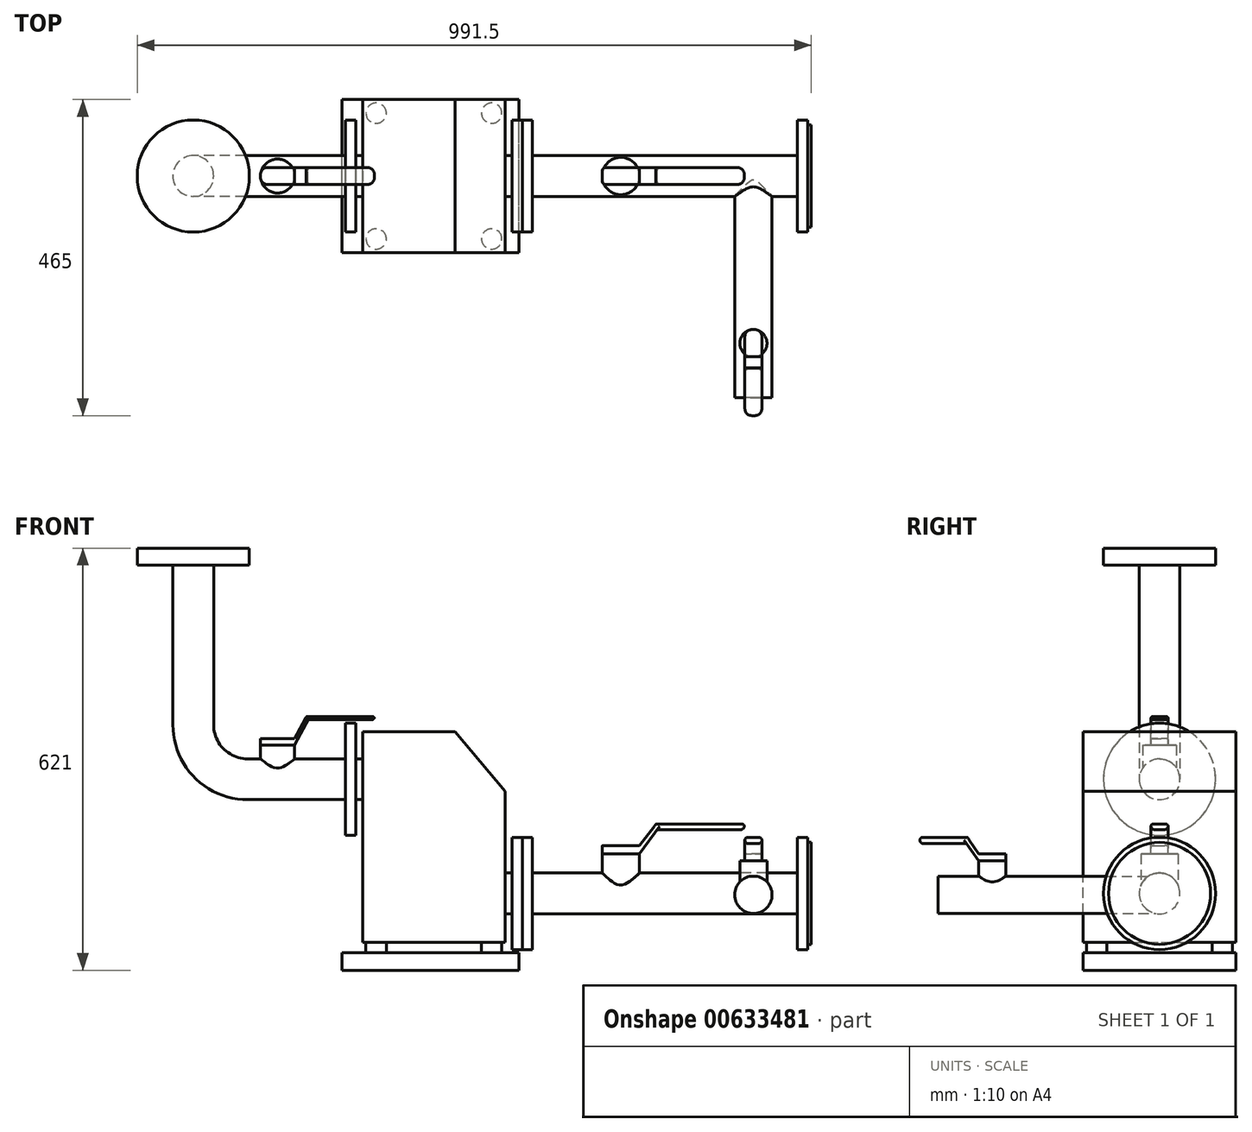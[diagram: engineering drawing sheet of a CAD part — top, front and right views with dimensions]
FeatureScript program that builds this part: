
annotation { "Feature Type Name" : "Feature", "Feature Type Description" : "" }
export const myFeature = defineFeature(function(context is Context, id is Id, definition is map)
    precondition{}
    {
        {
            var Q0;
            Q0=qCreatedBy(makeId("Front.planeOp"),FACE);
            var sketch = newSketch(context, id + "F0", { "sketchPlane" : qUnion([Q0])});
            skLineSegment(sketch, "E0.bottom", {"start": v(0, 0) * mm, "end": v(210, 0) * mm});
            skLineSegment(sketch, "E0.top", {"start": v(0, 310) * mm, "end": v(136.03, 310) * mm});
            skLineSegment(sketch, "E0.left", {"start": v(0, 0) * mm, "end": v(0, 310) * mm});
            skLineSegment(sketch, "E0.right", {"start": v(210, 0) * mm, "end": v(210, 222.5) * mm});
            skLineSegment(sketch, "E1", {"start": v(136.03, 310) * mm, "end": v(210, 222.5) * mm});
            skSolve(sketch);
        }
        {
            var Q0;
            Q0=makeQuery(id+"F0.imprint","IMPRINT",FACE,{"disambiguationData":[TD([[makeQuery(id+"F0.imprint","IMPRINT",EDGE,{"derivedFrom":sQuery(id+"F0.wireOp",EDGE,"E0.bottom")}),1.0]])]});
            extrude(context, id + "F1", {"entities" : qUnion([Q0]), "depth" : 225 * mm, "offsetDistance" : 25 * mm});
        }
        {
            var Q0;
            Q0=makeQuery(id+"F1.opExtrude","SWEPT_FACE",FACE,{"disambiguationData":[OSD([sQuery(id+"F0.wireOp",EDGE,"E0.right")])]});
            var sketch = newSketch(context, id + "F2", { "sketchPlane" : qUnion([Q0])});
            skCircle(sketch, "E2", {"center": v(-112.5, 72.05) * mm, "radius": 30 * mm});
            skPoint(sketch, "E2.centerSnap0", {"position": v(-112.5, 0) * mm});
            skCircle(sketch, "E3", {"center": v(-112.5, 72.05) * mm, "radius": 82.5 * mm});
            skSolve(sketch);
        }
        {
            var Q0;
            Q0=makeQuery(id+"F2.imprint","IMPRINT",FACE,{"disambiguationData":[TD([[makeQuery(id+"F2.imprint","IMPRINT",EDGE,{"derivedFrom":sQuery(id+"F2.wireOp",EDGE,"E2")}),1.0]])]});
            extrude(context, id + "F3", {"entities" : qUnion([Q0]), "operationType" : NewBodyOperationType.ADD, "depth" : 10 * mm, "offsetDistance" : 25 * mm});
        }
        {
            var Q0;
            Q0=makeQuery(id+"F3.opExtrude","CAP_FACE",FACE,{"disambiguationData":[OSD([sQuery(id+"F2.wireOp",EDGE,"E2")])],"isStart":false});
            var sketch = newSketch(context, id + "F4", { "sketchPlane" : qUnion([Q0])});
            skCircle(sketch, "E4", {"center": v(-112.5, 72.05) * mm, "radius": 82.5 * mm});
            skSolve(sketch);
        }
        {
            var Q0;
            Q0=makeQuery(id+"F4.imprint","IMPRINT",FACE,{"disambiguationData":[TD([[makeQuery(id+"F4.imprint","IMPRINT",EDGE,{"derivedFrom":sQuery(id+"F4.wireOp",EDGE,"E4")}),1.0]])]});
            var Q1;
            Q1=makeQuery(id+"F4.imprint","IMPRINT",FACE,{"disambiguationData":[TD([[makeQuery(id+"F4.imprint","IMPRINT",EDGE,{"derivedFrom":makeQuery(id+"F3.opExtrude","CAP_EDGE",EDGE,{"disambiguationData":[OSD([sQuery(id+"F2.wireOp",EDGE,"E2")])],"isStart":false})}),1.0]])]});
            extrude(context, id + "F5", {"entities" : qUnion([Q0, Q1]), "operationType" : NewBodyOperationType.ADD, "depth" : 15 * mm, "offsetDistance" : 25 * mm});
        }
        {
            var Q0;
            Q0=makeQuery(id+"F1.opExtrude","SWEPT_FACE",FACE,{"disambiguationData":[OSD([sQuery(id+"F0.wireOp",EDGE,"E0.left")])]});
            var sketch = newSketch(context, id + "F6", { "sketchPlane" : qUnion([Q0])});
            skCircle(sketch, "E5", {"center": v(112.5, 240) * mm, "radius": 30 * mm});
            skPoint(sketch, "E5.centerSnap0", {"position": v(112.5, 0) * mm});
            skSolve(sketch);
        }
        {
            var Q0;
            Q0=makeQuery(id+"F6.imprint","IMPRINT",FACE,{"disambiguationData":[TD([[makeQuery(id+"F6.imprint","IMPRINT",EDGE,{"derivedFrom":sQuery(id+"F6.wireOp",EDGE,"E5")}),1.0]])]});
            extrude(context, id + "F7", {"entities" : qUnion([Q0]), "operationType" : NewBodyOperationType.ADD, "depth" : 10 * mm, "offsetDistance" : 25 * mm});
        }
        {
            var Q0;
            Q0=makeQuery(id+"F7.opExtrude","CAP_FACE",FACE,{"disambiguationData":[OSD([sQuery(id+"F6.wireOp",EDGE,"E5")])],"isStart":false});
            var sketch = newSketch(context, id + "F8", { "sketchPlane" : qUnion([Q0])});
            skCircle(sketch, "E6", {"center": v(112.5, 240) * mm, "radius": 82.5 * mm});
            skSolve(sketch);
        }
        {
            var Q0;
            Q0 = qSketchRegion(id + "F8", true);
            extrude(context, id + "F9", {"entities" : qUnion([Q0]), "operationType" : NewBodyOperationType.ADD, "depth" : 15 * mm, "offsetDistance" : 25 * mm});
        }
        {
            var Q0;
            Q0=makeQuery(id+"F1.opExtrude","SWEPT_FACE",FACE,{"disambiguationData":[OSD([sQuery(id+"F0.wireOp",EDGE,"E0.bottom")])]});
            var sketch = newSketch(context, id + "F10", { "sketchPlane" : qUnion([Q0])});
            skCircle(sketch, "E7", {"center": v(20, 205) * mm, "radius": 15 * mm});
            skCircle(sketch, "E8.0.1.0", {"center": v(20, 20) * mm, "radius": 15 * mm});
            skCircle(sketch, "E8.1.0.0", {"center": v(190, 205) * mm, "radius": 15 * mm});
            skCircle(sketch, "E8.1.1.0", {"center": v(190, 20) * mm, "radius": 15 * mm});
            skLineSegment(sketch, "E8.direction1", {"start": v(20, 205) * mm, "end": v(190, 205) * mm, "construction": true});
            skLineSegment(sketch, "E8.direction2", {"start": v(20, 205) * mm, "end": v(20, 20) * mm, "construction": true});
            skSolve(sketch);
        }
        {
            var Q0;
            Q0 = qSketchRegion(id + "F10", true);
            extrude(context, id + "F11", {"entities" : qUnion([Q0]), "operationType" : NewBodyOperationType.ADD, "depth" : 15 * mm, "offsetDistance" : 25 * mm});
        }
        {
            var Q0;
            Q0=makeQuery(id+"F11.opExtrude","CAP_FACE",FACE,{"disambiguationData":[OSD([sQuery(id+"F10.wireOp",EDGE,"E7")])],"isStart":false});
            var sketch = newSketch(context, id + "F12", { "sketchPlane" : qUnion([Q0])});
            skPoint(sketch, "E9.bottom.start.orphan", {"position": v(0, 70.5) * mm});
            skLineSegment(sketch, "E10.bottom", {"start": v(-30, 225) * mm, "end": v(230, 225) * mm});
            skLineSegment(sketch, "E10.top", {"start": v(-30, 0) * mm, "end": v(230, 0) * mm});
            skLineSegment(sketch, "E10.left", {"start": v(-30, 225) * mm, "end": v(-30, 0) * mm});
            skLineSegment(sketch, "E10.right", {"start": v(230, 225) * mm, "end": v(230, 0) * mm});
            skSolve(sketch);
        }
        {
            var Q0;
            Q0 = qSketchRegion(id + "F12", true);
            extrude(context, id + "F13", {"entities" : qUnion([Q0]), "operationType" : NewBodyOperationType.ADD, "depth" : 26 * mm, "offsetDistance" : 25 * mm});
        }
        {
            var Q0;
            Q0=makeQuery(id+"F5.opExtrude","CAP_FACE",FACE,{"disambiguationData":[OSD([sQuery(id+"F4.wireOp",EDGE,"E4")])],"isStart":false});
            var sketch = newSketch(context, id + "F14", { "sketchPlane" : qUnion([Q0])});
            skCircle(sketch, "E11", {"center": v(-112.5, 72.05) * mm, "radius": 82.5 * mm});
            skSolve(sketch);
        }
        {
            var Q0;
            Q0=makeQuery(id+"F14.imprint","IMPRINT",FACE,{"disambiguationData":[TD([[makeQuery(id+"F14.imprint","IMPRINT",EDGE,{"derivedFrom":sQuery(id+"F14.wireOp",EDGE,"E11")}),1.0]])]});
            extrude(context, id + "F15", {"entities" : qUnion([Q0]), "depth" : 15 * mm, "offsetDistance" : 25 * mm});
        }
        {
            var Q0;
            Q0=makeQuery(id+"F15.opExtrude","CAP_FACE",FACE,{"disambiguationData":[OSD([sQuery(id+"F14.wireOp",EDGE,"E11")])],"isStart":false});
            var sketch = newSketch(context, id + "F16", { "sketchPlane" : qUnion([Q0])});
            skCircle(sketch, "E12", {"center": v(-112.5, 72.05) * mm, "radius": 30 * mm});
            skSolve(sketch);
        }
        {
            var Q0;
            Q0=makeQuery(id+"F16.imprint","IMPRINT",FACE,{"disambiguationData":[TD([[makeQuery(id+"F16.imprint","IMPRINT",EDGE,{"derivedFrom":sQuery(id+"F16.wireOp",EDGE,"E12")}),1.0]])]});
            extrude(context, id + "F17", {"entities" : qUnion([Q0]), "operationType" : NewBodyOperationType.ADD, "depth" : 390 * mm, "offsetDistance" : 25 * mm});
        }
        {
            var Q0;
            Q0=makeQuery(id+"F17.opExtrude","CAP_FACE",FACE,{"disambiguationData":[OSD([sQuery(id+"F16.wireOp",EDGE,"E12")])],"isStart":false});
            var sketch = newSketch(context, id + "F18", { "sketchPlane" : qUnion([Q0])});
            skCircle(sketch, "E13", {"center": v(-112.5, 72.05) * mm, "radius": 82.5 * mm});
            skSolve(sketch);
        }
        {
            var Q0;
            Q0=makeQuery(id+"F18.imprint","IMPRINT",FACE,{"disambiguationData":[TD([[makeQuery(id+"F18.imprint","IMPRINT",EDGE,{"derivedFrom":sQuery(id+"F18.wireOp",EDGE,"E13")}),1.0]])]});
            var Q1;
            Q1=makeQuery(id+"F18.imprint","IMPRINT",FACE,{"disambiguationData":[TD([[makeQuery(id+"F18.imprint","IMPRINT",EDGE,{"derivedFrom":makeQuery(id+"F17.opExtrude","CAP_EDGE",EDGE,{"disambiguationData":[OSD([sQuery(id+"F16.wireOp",EDGE,"E12")])],"isStart":false})}),1.0]])]});
            extrude(context, id + "F19", {"entities" : qUnion([Q0, Q1]), "operationType" : NewBodyOperationType.ADD, "depth" : 15 * mm, "offsetDistance" : 25 * mm});
        }
        {
            var Q0;
            Q0=makeQuery(id+"F19.opExtrude","CAP_FACE",FACE,{"disambiguationData":[OSD([sQuery(id+"F18.wireOp",EDGE,"E13")])],"isStart":false});
            var sketch = newSketch(context, id + "F20", { "sketchPlane" : qUnion([Q0])});
            skCircle(sketch, "E14", {"center": v(-112.5, 72.05) * mm, "radius": 75 * mm});
            skSolve(sketch);
        }
        {
            var Q0;
            Q0=makeQuery(id+"F20.imprint","IMPRINT",FACE,{"disambiguationData":[TD([[makeQuery(id+"F20.imprint","IMPRINT",EDGE,{"derivedFrom":sQuery(id+"F20.wireOp",EDGE,"E14")}),1.0]])]});
            extrude(context, id + "F21", {"entities" : qUnion([Q0]), "operationType" : NewBodyOperationType.ADD, "depth" : 5 * mm, "offsetDistance" : 25 * mm});
        }
        {
            var Q0;
            Q0=makeQuery(id+"F9.opExtrude","CAP_FACE",FACE,{"disambiguationData":[OSD([sQuery(id+"F8.wireOp",EDGE,"E6")])],"isStart":false});
            var sketch = newSketch(context, id + "F22", { "sketchPlane" : qUnion([Q0])});
            skCircle(sketch, "E15", {"center": v(112.5, 240) * mm, "radius": 30 * mm});
            skSolve(sketch);
        }
        {
            var Q0;
            Q0=qCreatedBy(makeId("Front.planeOp"),FACE);
            cPlane(context, id + "F23", {"entities" : qUnion([Q0]), "cplaneType" : CPlaneType.OFFSET, "offset" : 112.5 * mm, "width" : 150 * mm, "height" : 150 * mm});
        }
        {
            var Q0;
            Q0=qCreatedBy(id+"F23.planeOp",FACE);
            var sketch = newSketch(context, id + "F24", { "sketchPlane" : qUnion([Q0])});
            skPoint(sketch, "E16.0", {"position": v(-25, 240) * mm});
            skLineSegment(sketch, "E17", {"start": v(-25, 240) * mm, "end": v(-169, 240) * mm});
            skLineSegment(sketch, "E18", {"start": v(-249, 320) * mm, "end": v(-249, 580) * mm});
            skPoint(sketch, "E19.visualSharp", {"position": v(-249, 240) * mm});
            skArc(sketch, "E19.filletArc", {"start": v(-249, 320) * mm, "mid": v(-225.57, 263.43) * mm, "end": v(-169, 240) * mm});
            skSolve(sketch);
        }
        {
            var Q0;
            Q0=makeQuery(id+"F22.imprint","IMPRINT",FACE,{"disambiguationData":[TD([[makeQuery(id+"F22.imprint","IMPRINT",EDGE,{"derivedFrom":sQuery(id+"F22.wireOp",EDGE,"E15")}),1.0]])]});
            var Q1;
            Q1=sQuery(id+"F24.wireOp",EDGE,"E17");
            var Q2;
            Q2=sQuery(id+"F24.wireOp",EDGE,"E19.filletArc");
            var Q3;
            Q3=sQuery(id+"F24.wireOp",EDGE,"E18");
            sweep(context, id + "F25", {"operationType" : NewBodyOperationType.ADD, "profiles" : qUnion([Q0]), "path" : qUnion([Q1, Q2, Q3])});
        }
        {
            var Q0;
            Q0=makeQuery(id+"F25.opSweep","CAP_FACE",FACE,{"disambiguationData":[OSD([sQuery(id+"F22.wireOp",EDGE,"E15"),sQuery(id+"F24.wireOp",VERTEX,"E18.end")])],"isStart":false});
            var sketch = newSketch(context, id + "F26", { "sketchPlane" : qUnion([Q0])});
            skCircle(sketch, "E20", {"center": v(-249, -112.5) * mm, "radius": 82.5 * mm});
            skSolve(sketch);
        }
        {
            var Q0;
            Q0 = qSketchRegion(id + "F26", true);
            extrude(context, id + "F27", {"entities" : qUnion([Q0]), "operationType" : NewBodyOperationType.ADD, "oppositeDirection" : true, "depth" : 25 * mm, "offsetDistance" : 25 * mm});
        }
        {
            var Q0;
            Q0=qCreatedBy(makeId("Top.planeOp"),FACE);
            cPlane(context, id + "F28", {"entities" : qUnion([Q0]), "cplaneType" : CPlaneType.OFFSET, "offset" : 70 * mm, "width" : 150 * mm, "height" : 150 * mm});
        }
        {
            var Q0;
            Q0=qCreatedBy(id+"F28.planeOp",FACE);
            var sketch = newSketch(context, id + "F29", { "sketchPlane" : qUnion([Q0])});
            skCircle(sketch, "E21", {"center": v(380, -112.5) * mm, "radius": 27.5 * mm});
            skLineSegment(sketch, "E22", {"start": v(640, -142.5) * mm, "end": v(250, -142.5) * mm});
            skSolve(sketch);
        }
        {
            var Q0;
            Q0 = qSketchRegion(id + "F29", true);
            extrude(context, id + "F30", {"entities" : qUnion([Q0]), "operationType" : NewBodyOperationType.ADD, "depth" : 60 * mm, "offsetDistance" : 25 * mm});
        }
        {
            var Q0;
            Q0=qCreatedBy(id+"F23.planeOp",FACE);
            var sketch = newSketch(context, id + "F31", { "sketchPlane" : qUnion([Q0])});
            skLineSegment(sketch, "E23.0", {"start": v(352.5, 130) * mm, "end": v(407.5, 130) * mm});
            skLineSegment(sketch, "E24", {"start": v(352.5, 130) * mm, "end": v(352.5, 142) * mm});
            skLineSegment(sketch, "E25", {"start": v(352.5, 142) * mm, "end": v(407.5, 142) * mm});
            skLineSegment(sketch, "E26", {"start": v(407.5, 142) * mm, "end": v(431.57, 173.95) * mm});
            skLineSegment(sketch, "E27", {"start": v(431.57, 173.95) * mm, "end": v(561.57, 173.95) * mm});
            skLineSegment(sketch, "E28", {"start": v(561.57, 173.95) * mm, "end": v(561.57, 165.95) * mm});
            skLineSegment(sketch, "E29", {"start": v(561.57, 165.95) * mm, "end": v(433.57, 165.95) * mm});
            skLineSegment(sketch, "E30", {"start": v(433.57, 165.95) * mm, "end": v(407.5, 130) * mm});
            skSolve(sketch);
        }
        {
            var Q0;
            Q0=makeQuery(id+"F31.imprint","IMPRINT",FACE,{"disambiguationData":[TD([[makeQuery(id+"F31.imprint","IMPRINT",EDGE,{"derivedFrom":sQuery(id+"F31.wireOp",EDGE,"E23.0")}),1.0]])]});
            extrude(context, id + "F32", {"entities" : qUnion([Q0]), "operationType" : NewBodyOperationType.ADD, "endBound" : BoundingType.SYMMETRIC, "depth" : 25 * mm, "offsetDistance" : 25 * mm});
        }
        {
            var Q0;
            Q0=makeQuery(id+"F32.opExtrude","CAP_EDGE",EDGE,{"disambiguationData":[OSD([sQuery(id+"F31.wireOp",EDGE,"E28")])],"isStart":false});
            var Q1;
            Q1=makeQuery(id+"F32.opExtrude","CAP_EDGE",EDGE,{"disambiguationData":[OSD([sQuery(id+"F31.wireOp",EDGE,"E28")])],"isStart":true});
            fillet(context, id + "F33", {"entities" : qUnion([Q0, Q1]), "radius" : 10 * mm, "tangentPropagation" : true, "allowEdgeOverflow" : false});
        }
        {
            var Q0;
            Q0=makeQuery(id+"F32.opExtrude","CAP_EDGE",EDGE,{"disambiguationData":[OSD([sQuery(id+"F31.wireOp",EDGE,"E27")])],"isStart":false});
            fillet(context, id + "F34", {"entities" : qUnion([Q0]), "radius" : 3 * mm, "tangentPropagation" : true, "allowEdgeOverflow" : false});
        }
        {
            var Q0;
            Q0=makeQuery(id+"F32.opExtrude","CAP_EDGE",EDGE,{"disambiguationData":[OSD([sQuery(id+"F31.wireOp",EDGE,"E29")])],"isStart":false});
            fillet(context, id + "F35", {"entities" : qUnion([Q0]), "radius" : 5 * mm, "tangentPropagation" : true, "allowEdgeOverflow" : false});
        }
        {
            var Q0;
            Q0=makeQuery(id+"F32.opExtrude","CAP_EDGE",EDGE,{"disambiguationData":[OSD([sQuery(id+"F31.wireOp",EDGE,"E24")])],"isStart":false});
            var Q1;
            Q1=makeQuery(id+"F32.opExtrude","CAP_EDGE",EDGE,{"disambiguationData":[OSD([sQuery(id+"F31.wireOp",EDGE,"E24")])],"isStart":true});
            fillet(context, id + "F36", {"entities" : qUnion([Q0, Q1]), "radius" : 5 * mm, "tangentPropagation" : true, "allowEdgeOverflow" : false});
        }
        {
            var Q0;
            Q0=qCreatedBy(makeId("Top.planeOp"),FACE);
            cPlane(context, id + "F37", {"entities" : qUnion([Q0]), "cplaneType" : CPlaneType.OFFSET, "offset" : 240 * mm, "width" : 150 * mm, "height" : 150 * mm});
        }
        {
            var Q0;
            Q0=qCreatedBy(id+"F37.planeOp",FACE);
            var sketch = newSketch(context, id + "F38", { "sketchPlane" : qUnion([Q0])});
            skCircle(sketch, "E31", {"center": v(-125, -112.5) * mm, "radius": 25 * mm});
            skSolve(sketch);
        }
        {
            var Q0;
            Q0 = qSketchRegion(id + "F38", true);
            extrude(context, id + "F39", {"entities" : qUnion([Q0]), "operationType" : NewBodyOperationType.ADD, "depth" : 50 * mm, "offsetDistance" : 25 * mm});
        }
        {
            var Q0;
            Q0=qCreatedBy(id+"F23.planeOp",FACE);
            var sketch = newSketch(context, id + "F40", { "sketchPlane" : qUnion([Q0])});
            skLineSegment(sketch, "E32.0", {"start": v(-150, 290) * mm, "end": v(-100, 290) * mm});
            skLineSegment(sketch, "E33", {"start": v(-150, 290) * mm, "end": v(-150, 300) * mm});
            skLineSegment(sketch, "E34", {"start": v(-150, 300) * mm, "end": v(-100, 300) * mm});
            skLineSegment(sketch, "E35", {"start": v(-100, 300) * mm, "end": v(-82.68, 332.04) * mm});
            skLineSegment(sketch, "E36", {"start": v(-82.68, 332.04) * mm, "end": v(17.32, 332.04) * mm});
            skLineSegment(sketch, "E37", {"start": v(17.32, 332.04) * mm, "end": v(17.32, 327.41) * mm});
            skLineSegment(sketch, "E38", {"start": v(17.32, 327.41) * mm, "end": v(-80.12, 327.41) * mm});
            skLineSegment(sketch, "E39", {"start": v(-80.12, 327.41) * mm, "end": v(-100, 290) * mm});
            skSolve(sketch);
        }
        {
            var Q0;
            Q0 = qSketchRegion(id + "F40", true);
            extrude(context, id + "F41", {"entities" : qUnion([Q0]), "operationType" : NewBodyOperationType.ADD, "endBound" : BoundingType.SYMMETRIC, "depth" : 25 * mm, "offsetDistance" : 25 * mm});
        }
        {
            var Q0;
            Q0=makeQuery(id+"F41.opExtrude","CAP_EDGE",EDGE,{"disambiguationData":[OSD([sQuery(id+"F40.wireOp",EDGE,"E37")])],"isStart":false});
            var Q1;
            Q1=makeQuery(id+"F41.opExtrude","CAP_EDGE",EDGE,{"disambiguationData":[OSD([sQuery(id+"F40.wireOp",EDGE,"E37")])],"isStart":true});
            fillet(context, id + "F42", {"entities" : qUnion([Q0, Q1]), "radius" : 10 * mm, "tangentPropagation" : true, "allowEdgeOverflow" : false});
        }
        {
            var Q0;
            Q0=makeQuery(id+"F41.opExtrude","CAP_EDGE",EDGE,{"disambiguationData":[OSD([sQuery(id+"F40.wireOp",EDGE,"E36")])],"isStart":false});
            fillet(context, id + "F43", {"entities" : qUnion([Q0]), "radius" : 2 * mm, "tangentPropagation" : true, "allowEdgeOverflow" : false});
        }
        {
            var Q0;
            Q0=makeQuery(id+"F41.opExtrude","CAP_EDGE",EDGE,{"disambiguationData":[OSD([sQuery(id+"F40.wireOp",EDGE,"E38")])],"isStart":false});
            fillet(context, id + "F44", {"entities" : qUnion([Q0]), "radius" : 5 * mm, "tangentPropagation" : true, "allowEdgeOverflow" : false});
        }
        {
            var Q0;
            Q0=makeQuery(id+"F41.opExtrude","CAP_EDGE",EDGE,{"disambiguationData":[OSD([sQuery(id+"F40.wireOp",EDGE,"E33")])],"isStart":false});
            var Q1;
            Q1=makeQuery(id+"F41.opExtrude","CAP_EDGE",EDGE,{"disambiguationData":[OSD([sQuery(id+"F40.wireOp",EDGE,"E33")])],"isStart":true});
            fillet(context, id + "F45", {"entities" : qUnion([Q0, Q1]), "radius" : 10 * mm, "tangentPropagation" : true, "allowEdgeOverflow" : false});
        }
        {
            var Q0;
            Q0=qCreatedBy(id+"F23.planeOp",FACE);
            var sketch = newSketch(context, id + "F46", { "sketchPlane" : qUnion([Q0])});
            skCircle(sketch, "E40", {"center": v(575, 70) * mm, "radius": 27.5 * mm});
            skSolve(sketch);
        }
        {
            var Q0;
            Q0 = qSketchRegion(id + "F46", true);
            extrude(context, id + "F47", {"entities" : qUnion([Q0]), "operationType" : NewBodyOperationType.ADD, "depth" : 326 * mm, "offsetDistance" : 25 * mm});
        }
        {
            var Q0;
            Q0=qCreatedBy(id+"F28.planeOp",FACE);
            var sketch = newSketch(context, id + "F48", { "sketchPlane" : qUnion([Q0])});
            skCircle(sketch, "E41", {"center": v(575, -358.5) * mm, "radius": 20 * mm});
            skLineSegment(sketch, "E42", {"start": v(602.5, -142.43) * mm, "end": v(602.5, -438.5) * mm});
            skSolve(sketch);
        }
        {
            var Q0;
            Q0 = qSketchRegion(id + "F48", true);
            extrude(context, id + "F49", {"entities" : qUnion([Q0]), "operationType" : NewBodyOperationType.ADD, "depth" : 50 * mm, "offsetDistance" : 25 * mm});
        }
        {
            var Q0;
            Q0=makeQuery(id+"F21.opExtrude","CAP_FACE",FACE,{"disambiguationData":[OSD([sQuery(id+"F20.wireOp",EDGE,"E14")])],"isStart":false});
            cPlane(context, id + "F50", {"entities" : qUnion([Q0]), "cplaneType" : CPlaneType.OFFSET, "offset" : 85 * mm, "oppositeDirection" : true, "width" : 150 * mm, "height" : 150 * mm});
        }
        {
            var Q0;
            Q0=qCreatedBy(id+"F50.planeOp",FACE);
            var sketch = newSketch(context, id + "F51", { "sketchPlane" : qUnion([Q0])});
            skLineSegment(sketch, "E43.0", {"start": v(-378.5, 120) * mm, "end": v(-338.5, 120) * mm});
            skLineSegment(sketch, "E44", {"start": v(-338.5, 120) * mm, "end": v(-338.5, 130) * mm});
            skLineSegment(sketch, "E45", {"start": v(-338.5, 130) * mm, "end": v(-378.5, 130) * mm});
            skLineSegment(sketch, "E46", {"start": v(-378.5, 130) * mm, "end": v(-395, 154.52) * mm});
            skLineSegment(sketch, "E47", {"start": v(-395, 154.52) * mm, "end": v(-465, 154.52) * mm});
            skLineSegment(sketch, "E48", {"start": v(-465, 154.52) * mm, "end": v(-465, 145.28) * mm});
            skLineSegment(sketch, "E49", {"start": v(-465, 145.28) * mm, "end": v(-396.85, 145.28) * mm});
            skLineSegment(sketch, "E50", {"start": v(-396.85, 145.28) * mm, "end": v(-378.5, 120) * mm});
            skSolve(sketch);
        }
        {
            var Q0;
            Q0=makeQuery(id+"F51.imprint","IMPRINT",FACE,{"disambiguationData":[TD([[makeQuery(id+"F51.imprint","IMPRINT",EDGE,{"derivedFrom":sQuery(id+"F51.wireOp",EDGE,"E43.0")}),1.0]])]});
            extrude(context, id + "F52", {"entities" : qUnion([Q0]), "operationType" : NewBodyOperationType.ADD, "endBound" : BoundingType.SYMMETRIC, "depth" : 25 * mm, "offsetDistance" : 25 * mm});
        }
        {
            var Q0;
            Q0=makeQuery(id+"F52.opExtrude","CAP_EDGE",EDGE,{"disambiguationData":[OSD([sQuery(id+"F51.wireOp",EDGE,"E48")])],"isStart":false});
            var Q1;
            Q1=makeQuery(id+"F52.opExtrude","CAP_EDGE",EDGE,{"disambiguationData":[OSD([sQuery(id+"F51.wireOp",EDGE,"E48")])],"isStart":true});
            fillet(context, id + "F53", {"entities" : qUnion([Q0, Q1]), "radius" : 10 * mm, "tangentPropagation" : true, "allowEdgeOverflow" : false});
        }
        {
            var Q0;
            Q0=makeQuery(id+"F52.opExtrude","CAP_EDGE",EDGE,{"disambiguationData":[OSD([sQuery(id+"F51.wireOp",EDGE,"E47")])],"isStart":false});
            fillet(context, id + "F54", {"entities" : qUnion([Q0]), "radius" : 4 * mm, "tangentPropagation" : true, "allowEdgeOverflow" : false});
        }
        {
            var Q0;
            Q0=makeQuery(id+"F52.opExtrude","CAP_EDGE",EDGE,{"disambiguationData":[OSD([sQuery(id+"F51.wireOp",EDGE,"E49")])],"isStart":false});
            fillet(context, id + "F55", {"entities" : qUnion([Q0]), "radius" : 5 * mm, "tangentPropagation" : true, "allowEdgeOverflow" : false});
        }
        {
            var Q0;
            Q0=makeQuery(id+"F52.opExtrude","CAP_EDGE",EDGE,{"disambiguationData":[OSD([sQuery(id+"F51.wireOp",EDGE,"E44")])],"isStart":false});
            var Q1;
            Q1=makeQuery(id+"F52.opExtrude","CAP_EDGE",EDGE,{"disambiguationData":[OSD([sQuery(id+"F51.wireOp",EDGE,"E44")])],"isStart":true});
            fillet(context, id + "F56", {"entities" : qUnion([Q0, Q1]), "radius" : 10 * mm, "tangentPropagation" : true, "allowEdgeOverflow" : false});
        }
    });
